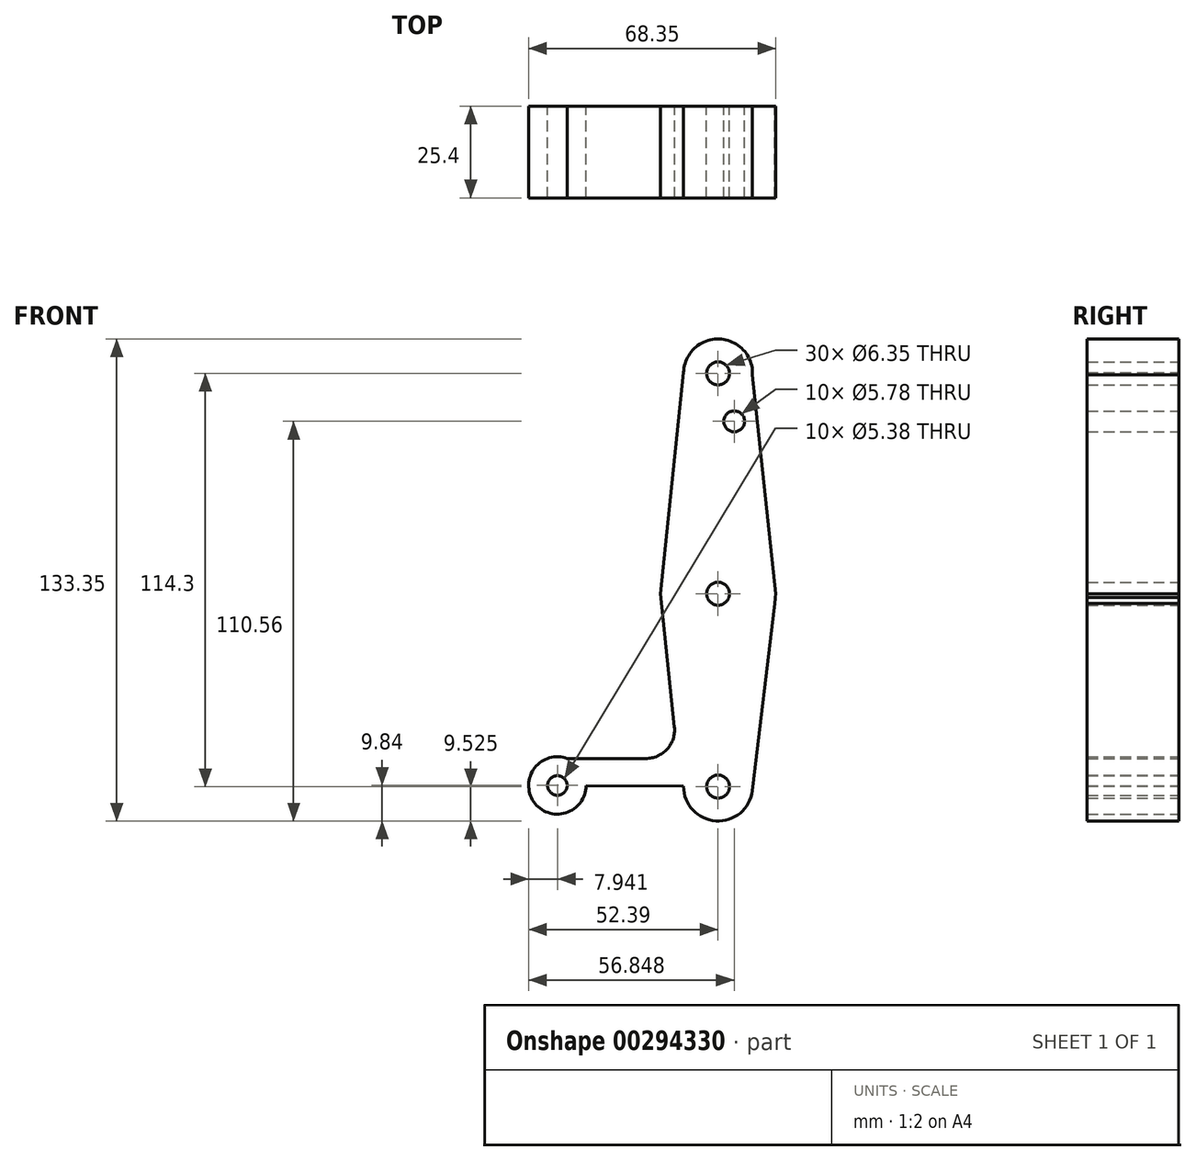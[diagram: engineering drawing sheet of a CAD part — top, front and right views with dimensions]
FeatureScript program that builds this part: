
annotation { "Feature Type Name" : "Feature", "Feature Type Description" : "" }
export const myFeature = defineFeature(function(context is Context, id is Id, definition is map)
    precondition{}
    {
        {
            var Q0;
            Q0=qCreatedBy(makeId("Front.planeOp"),FACE);
            var sketch = newSketch(context, id + "F0", { "sketchPlane" : qUnion([Q0])});
            skCircle(sketch, "E0", {"center": v(0, 0) * mm, "radius": 15.88 * mm});
            skCircle(sketch, "E1", {"center": v(0, 60.93) * mm, "radius": 9.53 * mm});
            skCircle(sketch, "E2", {"center": v(0, -53.37) * mm, "radius": 9.53 * mm});
            skCircle(sketch, "E3", {"center": v(-44.45, -53.05) * mm, "radius": 7.94 * mm});
            skLineSegment(sketch, "E4", {"start": v(0, 60.93) * mm, "end": v(0, -53.37) * mm});
            skLineSegment(sketch, "E5", {"start": v(0, -53.37) * mm, "end": v(-44.45, -53.05) * mm});
            skLineSegment(sketch, "E6", {"start": v(9.52, 60.59) * mm, "end": v(15.96, 0) * mm});
            skLineSegment(sketch, "E7", {"start": v(-9.52, 61.18) * mm, "end": v(-15.96, 0) * mm});
            skLineSegment(sketch, "E8", {"start": v(15.96, 0) * mm, "end": v(9.46, -54.5) * mm});
            skLineSegment(sketch, "E9", {"start": v(-15.96, 0) * mm, "end": v(-12.09, -36.83) * mm});
            skLineSegment(sketch, "E10", {"start": v(-20, -45.6) * mm, "end": v(-44.45, -45.6) * mm});
            skLineSegment(sketch, "E11", {"start": v(0, -62.9) * mm, "end": v(-44.45, -61) * mm});
            skArc(sketch, "E12.filletArc", {"start": v(-20, -45.6) * mm, "mid": v(-14.08, -42.98) * mm, "end": v(-12.09, -36.83) * mm});
            skCircle(sketch, "E13", {"center": v(0, 60.93) * mm, "radius": 3.18 * mm});
            skCircle(sketch, "E14", {"center": v(4.46, 47.67) * mm, "radius": 2.9 * mm});
            skCircle(sketch, "E15", {"center": v(0, 0) * mm, "radius": 3.18 * mm});
            skCircle(sketch, "E16", {"center": v(0, -53.37) * mm, "radius": 3.18 * mm});
            skCircle(sketch, "E17", {"center": v(-44.45, -53.05) * mm, "radius": 2.7 * mm});
            skSolve(sketch);
        }
        {
            var Q0;
            {var subQ0=sQuery(id+"F0.wireOp",EDGE,"E7");var subQ1=sQuery(id+"F0.wireOp",EDGE,"E0");var subQ2=makeQuery(id+"F0.imprint","INTERSECT",VERTEX,{"derivedFrom":[subQ1,subQ0]});Q0=makeQuery(id+"F0.imprint","IMPRINT",FACE,{"disambiguationData":[TD([[makeQuery(id+"F0.imprint","IMPRINT",EDGE,{"disambiguationData":[TD([[subQ2,-1.0]])],"derivedFrom":subQ1}),-1.0]])]});}
            var Q1;
            {var subQ0=sQuery(id+"F0.wireOp",EDGE,"E8");var subQ1=sQuery(id+"F0.wireOp",EDGE,"E0");var subQ2=makeQuery(id+"F0.imprint","INTERSECT",VERTEX,{"disambiguationData":[OD(0.0)],"derivedFrom":[subQ1,subQ0]});Q1=makeQuery(id+"F0.imprint","IMPRINT",FACE,{"disambiguationData":[TD([[makeQuery(id+"F0.imprint","IMPRINT",EDGE,{"disambiguationData":[TD([[subQ2,-1.0]])],"derivedFrom":subQ1}),1.0]])]});}
            var Q2;
            {var subQ0=sQuery(id+"F0.wireOp",EDGE,"E6");var subQ1=sQuery(id+"F0.wireOp",EDGE,"E0");var subQ2=makeQuery(id+"F0.imprint","INTERSECT",VERTEX,{"derivedFrom":[subQ1,subQ0]});Q2=makeQuery(id+"F0.imprint","IMPRINT",FACE,{"disambiguationData":[TD([[makeQuery(id+"F0.imprint","IMPRINT",EDGE,{"disambiguationData":[TD([[subQ2,1.0]])],"derivedFrom":subQ1}),-1.0]])]});}
            var Q3;
            {var subQ0=sQuery(id+"F0.wireOp",EDGE,"E11");var subQ1=sQuery(id+"F0.wireOp",EDGE,"E2");var subQ2=makeQuery(id+"F0.imprint","INTERSECT",VERTEX,{"disambiguationData":[OD(0.0)],"derivedFrom":[subQ1,subQ0]});Q3=makeQuery(id+"F0.imprint","IMPRINT",FACE,{"disambiguationData":[TD([[makeQuery(id+"F0.imprint","IMPRINT",EDGE,{"disambiguationData":[TD([[subQ2,1.0]])],"derivedFrom":subQ1}),1.0]])]});}
            var Q4;
            Q4=makeQuery(id+"F0.imprint","IMPRINT",FACE,{"disambiguationData":[TD([[makeQuery(id+"F0.imprint","IMPRINT",EDGE,{"derivedFrom":sQuery(id+"F0.wireOp",EDGE,"E17")}),-1.0]])]});
            var Q5;
            {var subQ0=sQuery(id+"F0.wireOp",EDGE,"E7");var subQ1=sQuery(id+"F0.wireOp",EDGE,"E0");var subQ2=makeQuery(id+"F0.imprint","INTERSECT",VERTEX,{"derivedFrom":[subQ1,subQ0]});Q5=makeQuery(id+"F0.imprint","IMPRINT",FACE,{"disambiguationData":[TD([[makeQuery(id+"F0.imprint","IMPRINT",EDGE,{"disambiguationData":[TD([[subQ2,1.0]])],"derivedFrom":subQ1}),-1.0]])]});}
            var Q6;
            {var subQ0=sQuery(id+"F0.wireOp",EDGE,"E8");var subQ1=sQuery(id+"F0.wireOp",EDGE,"E0");var subQ2=makeQuery(id+"F0.imprint","INTERSECT",VERTEX,{"disambiguationData":[OD(0.0)],"derivedFrom":[subQ1,subQ0]});Q6=makeQuery(id+"F0.imprint","IMPRINT",FACE,{"disambiguationData":[TD([[makeQuery(id+"F0.imprint","IMPRINT",EDGE,{"disambiguationData":[TD([[subQ2,1.0]])],"derivedFrom":subQ1}),-1.0]])]});}
            var Q7;
            Q7=makeQuery(id+"F0.imprint","IMPRINT",FACE,{"disambiguationData":[TD([[makeQuery(id+"F0.imprint","IMPRINT",EDGE,{"derivedFrom":sQuery(id+"F0.wireOp",EDGE,"E13")}),-1.0]])]});
            var Q8;
            {var subQ0=sQuery(id+"F0.wireOp",EDGE,"E5");var subQ1=sQuery(id+"F0.wireOp",EDGE,"E2");var subQ2=makeQuery(id+"F0.imprint","INTERSECT",VERTEX,{"derivedFrom":[subQ1,subQ0]});Q8=makeQuery(id+"F0.imprint","IMPRINT",FACE,{"disambiguationData":[TD([[makeQuery(id+"F0.imprint","IMPRINT",EDGE,{"disambiguationData":[TD([[subQ2,1.0]])],"derivedFrom":subQ1}),1.0]])]});}
            var Q9;
            Q9=makeQuery(id+"F0.imprint","IMPRINT",FACE,{"disambiguationData":[TD([[makeQuery(id+"F0.imprint","IMPRINT",EDGE,{"derivedFrom":sQuery(id+"F0.wireOp",EDGE,"E14")}),-1.0]])]});
            var Q10;
            {var subQ11=sQuery(id+"F0.wireOp",EDGE,"E12.filletArc");Q10=makeQuery(id+"F0.imprint","IMPRINT",FACE,{"disambiguationData":[TD([[makeQuery(id+"F0.imprint","IMPRINT",EDGE,{"derivedFrom":subQ11}),-1.0]])]});}
            var Q11;
            {var subQ1=sQuery(id+"F0.wireOp",EDGE,"E0");var subQ7=makeQuery(id+"F0.imprint","INTERSECT",VERTEX,{"derivedFrom":[subQ1,sQuery(id+"F0.wireOp",EDGE,"E7")]});Q11=makeQuery(id+"F0.imprint","IMPRINT",FACE,{"disambiguationData":[TD([[makeQuery(id+"F0.imprint","IMPRINT",EDGE,{"disambiguationData":[TD([[subQ7,1.0]])],"derivedFrom":subQ1}),1.0]])]});}
            var Q12;
            {var subQ1=sQuery(id+"F0.wireOp",EDGE,"E0");var subQ5=makeQuery(id+"F0.imprint","INTERSECT",VERTEX,{"derivedFrom":[subQ1,sQuery(id+"F0.wireOp",EDGE,"E6")]});Q12=makeQuery(id+"F0.imprint","IMPRINT",FACE,{"disambiguationData":[TD([[makeQuery(id+"F0.imprint","IMPRINT",EDGE,{"disambiguationData":[TD([[subQ5,-1.0]])],"derivedFrom":subQ1}),1.0]])]});}
            var Q13;
            {var subQ1=sQuery(id+"F0.wireOp",EDGE,"E2");var subQ5=sQuery(id+"F0.wireOp",EDGE,"E11");var subQ6=makeQuery(id+"F0.imprint","INTERSECT",VERTEX,{"disambiguationData":[OD(1.0)],"derivedFrom":[subQ1,subQ5]});Q13=makeQuery(id+"F0.imprint","IMPRINT",FACE,{"disambiguationData":[TD([[makeQuery(id+"F0.imprint","IMPRINT",EDGE,{"disambiguationData":[TD([[subQ6,1.0]])],"derivedFrom":subQ1}),1.0]])]});}
            extrude(context, id + "F1", {"entities" : qUnion([Q0, Q1, Q2, Q3, Q4, Q5, Q6, Q7, Q8, Q9, Q10, Q11, Q12, Q13]), "depth" : 25.4 * mm});
        }
    });
